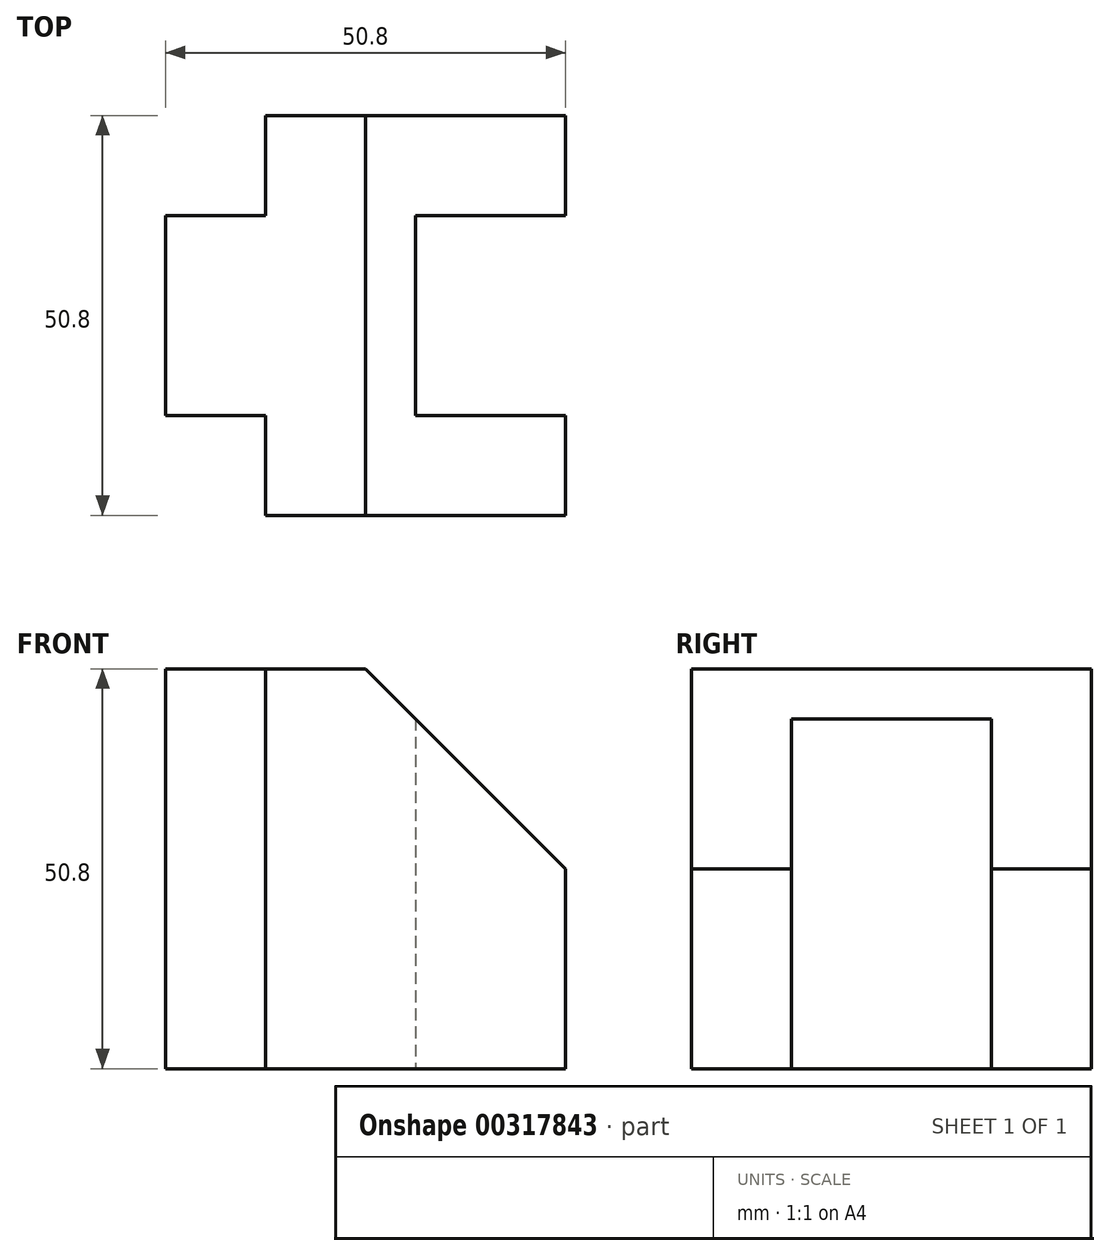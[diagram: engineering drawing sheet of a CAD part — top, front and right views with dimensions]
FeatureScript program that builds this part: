
annotation { "Feature Type Name" : "Feature", "Feature Type Description" : "" }
export const myFeature = defineFeature(function(context is Context, id is Id, definition is map)
    precondition{}
    {
        {
            var Q0;
            Q0=qCreatedBy(makeId("Front.planeOp"),FACE);
            var sketch = newSketch(context, id + "F0", { "sketchPlane" : qUnion([Q0])});
            skLineSegment(sketch, "E0", {"start": v(0, 0) * mm, "end": v(50.8, 0) * mm});
            skLineSegment(sketch, "E1", {"start": v(50.8, 0) * mm, "end": v(50.8, 50.8) * mm});
            skLineSegment(sketch, "E2", {"start": v(50.8, 50.8) * mm, "end": v(0, 50.8) * mm});
            skLineSegment(sketch, "E3", {"start": v(0, 50.8) * mm, "end": v(0, 0) * mm});
            skSolve(sketch);
        }
        {
            var Q0;
            Q0 = qSketchRegion(id + "F0", true);
            extrude(context, id + "F1", {"entities" : qUnion([Q0]), "endBound" : BoundingType.SYMMETRIC, "depth" : 50.8 * mm});
        }
        {
            var Q0;
            Q0=qCreatedBy(makeId("Front.planeOp"),FACE);
            var sketch = newSketch(context, id + "F2", { "sketchPlane" : qUnion([Q0])});
            skLineSegment(sketch, "E4", {"start": v(50.8, 50.8) * mm, "end": v(25.4, 50.8) * mm});
            skLineSegment(sketch, "E5", {"start": v(25.4, 50.8) * mm, "end": v(50.8, 25.4) * mm});
            skLineSegment(sketch, "E6", {"start": v(50.8, 25.4) * mm, "end": v(50.8, 50.8) * mm});
            skSolve(sketch);
        }
        {
            var Q0;
            Q0 = qSketchRegion(id + "F2", true);
            extrude(context, id + "F3", {"entities" : qUnion([Q0]), "operationType" : NewBodyOperationType.REMOVE, "endBound" : BoundingType.THROUGH_ALL, "oppositeDirection" : true, "depth" : 25.4 * mm, "hasSecondDirection" : true, "secondDirectionBound" : SecondDirectionBoundingType.THROUGH_ALL, "secondDirectionOppositeDirection" : false, "secondDirectionDepth" : 25.4 * mm});
        }
        {
            var Q0;
            Q0=qCreatedBy(makeId("Top.planeOp"),FACE);
            var sketch = newSketch(context, id + "F4", { "sketchPlane" : qUnion([Q0])});
            skLineSegment(sketch, "E7.bottom", {"start": v(0, 25.4) * mm, "end": v(12.7, 25.4) * mm});
            skLineSegment(sketch, "E7.top", {"start": v(0, 12.7) * mm, "end": v(12.7, 12.7) * mm});
            skLineSegment(sketch, "E7.left", {"start": v(0, 25.4) * mm, "end": v(0, 12.7) * mm});
            skLineSegment(sketch, "E7.right", {"start": v(12.7, 25.4) * mm, "end": v(12.7, 12.7) * mm});
            skLineSegment(sketch, "E8.bottom", {"start": v(0, -25.4) * mm, "end": v(12.7, -25.4) * mm});
            skLineSegment(sketch, "E8.top", {"start": v(0, -12.7) * mm, "end": v(12.7, -12.7) * mm});
            skLineSegment(sketch, "E8.left", {"start": v(0, -25.4) * mm, "end": v(0, -12.7) * mm});
            skLineSegment(sketch, "E8.right", {"start": v(12.7, -25.4) * mm, "end": v(12.7, -12.7) * mm});
            skLineSegment(sketch, "E9.bottom", {"start": v(50.8, 12.7) * mm, "end": v(31.75, 12.7) * mm});
            skLineSegment(sketch, "E9.top", {"start": v(50.8, -12.7) * mm, "end": v(31.75, -12.7) * mm});
            skLineSegment(sketch, "E9.left", {"start": v(50.8, 12.7) * mm, "end": v(50.8, -12.7) * mm});
            skLineSegment(sketch, "E9.right", {"start": v(31.75, 12.7) * mm, "end": v(31.75, -12.7) * mm});
            skSolve(sketch);
        }
        {
            var Q0;
            Q0 = qSketchRegion(id + "F4", true);
            extrude(context, id + "F5", {"entities" : qUnion([Q0]), "operationType" : NewBodyOperationType.REMOVE, "endBound" : BoundingType.THROUGH_ALL, "depth" : 25.4 * mm});
        }
    });
